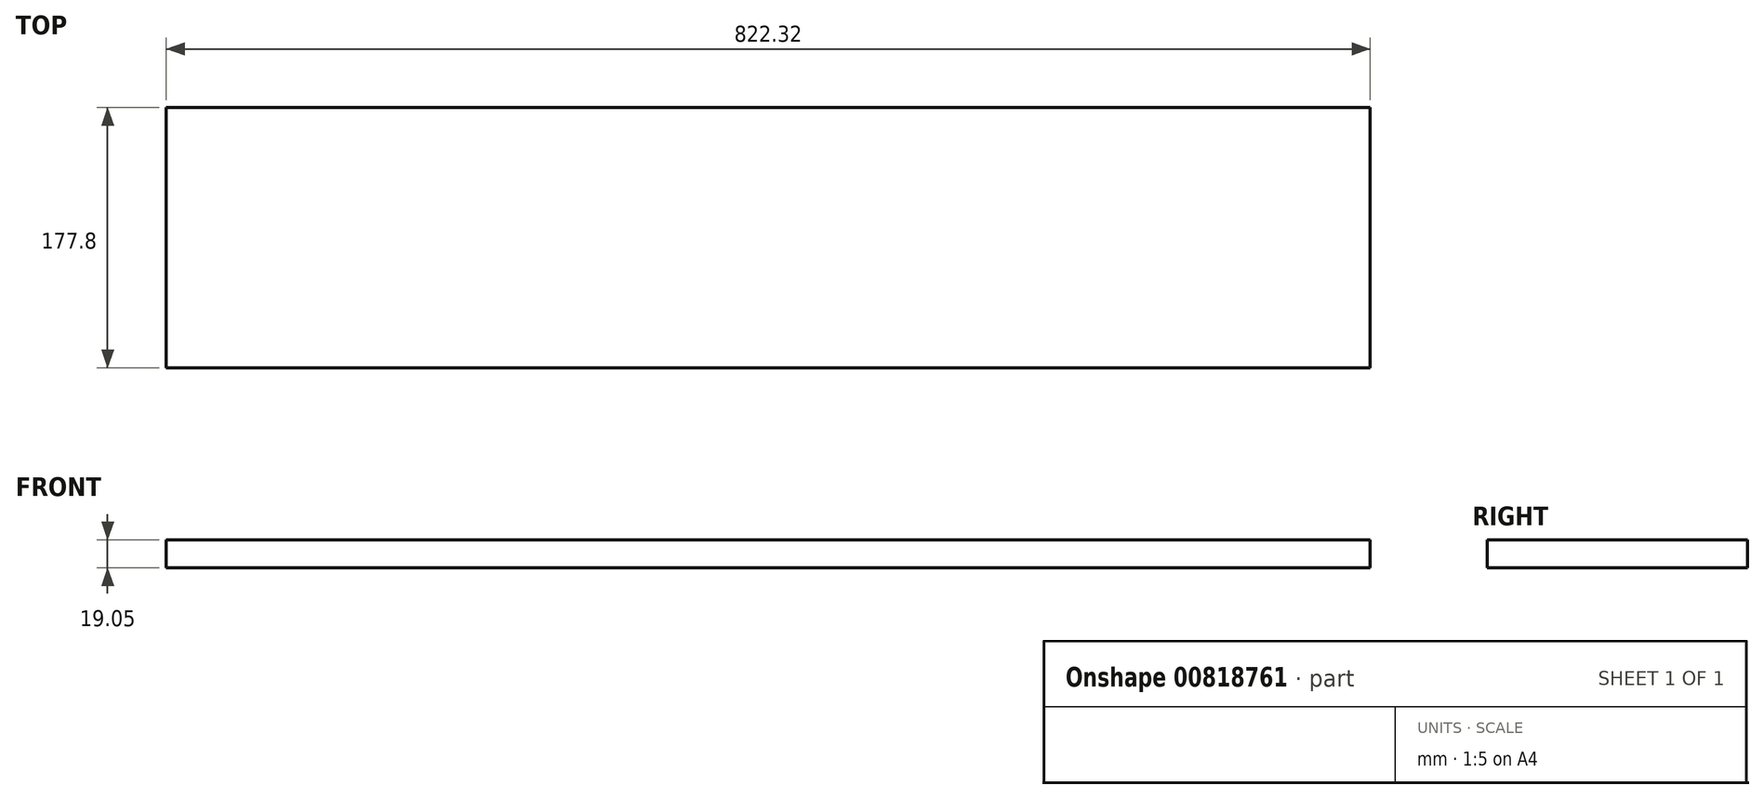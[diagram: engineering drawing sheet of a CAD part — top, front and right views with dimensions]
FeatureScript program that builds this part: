
annotation { "Feature Type Name" : "Feature", "Feature Type Description" : "" }
export const myFeature = defineFeature(function(context is Context, id is Id, definition is map)
    precondition{}
    {
        {
            var Q0;
            Q0=qCreatedBy(makeId("Top.planeOp"),FACE);
            var sketch = newSketch(context, id + "F0", { "sketchPlane" : qUnion([Q0])});
            skLineSegment(sketch, "E0.bottom", {"start": v(411.16, 88.9) * mm, "end": v(-411.16, 88.9) * mm});
            skLineSegment(sketch, "E0.top", {"start": v(411.16, -88.9) * mm, "end": v(-411.16, -88.9) * mm});
            skLineSegment(sketch, "E0.left", {"start": v(411.16, 88.9) * mm, "end": v(411.16, -88.9) * mm});
            skLineSegment(sketch, "E0.right", {"start": v(-411.16, 88.9) * mm, "end": v(-411.16, -88.9) * mm});
            skPoint(sketch, "E0.middle", {"position": v(0, 0) * mm});
            skSolve(sketch);
        }
        {
            var Q0;
            Q0=makeQuery(id+"F0.imprint","IMPRINT",FACE,{"disambiguationData":[TD([[makeQuery(id+"F0.imprint","IMPRINT",EDGE,{"derivedFrom":sQuery(id+"F0.wireOp",EDGE,"E0.bottom")}),1.0]])]});
            extrude(context, id + "F1", {"entities" : qUnion([Q0]), "depth" : 19.05 * mm, "offsetDistance" : 25.4 * mm});
        }
    });
